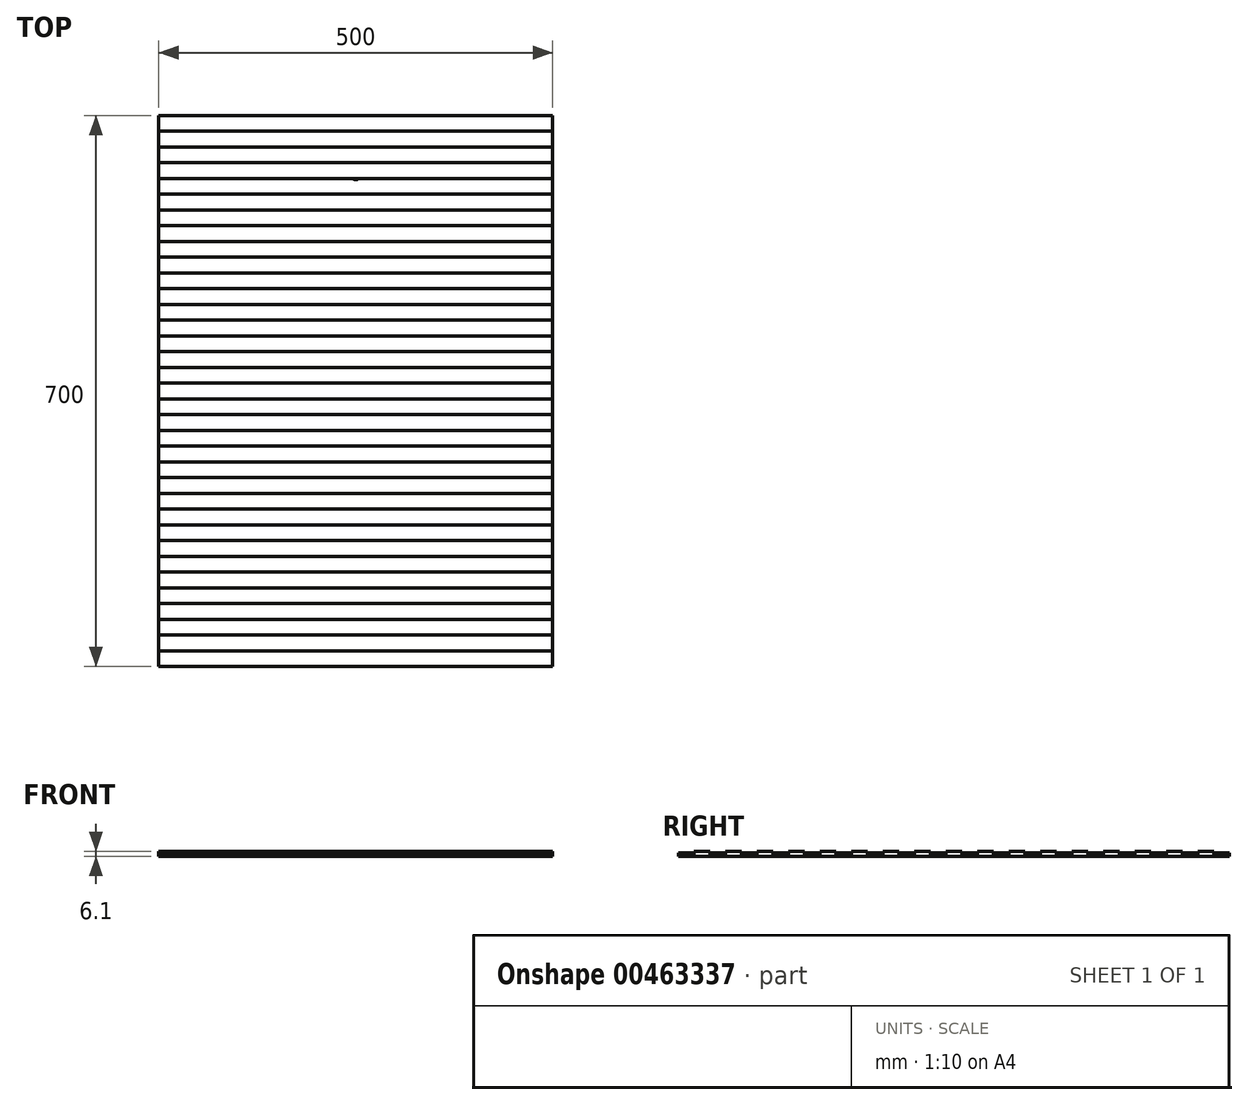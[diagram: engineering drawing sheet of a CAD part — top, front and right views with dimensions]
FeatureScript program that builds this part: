
annotation { "Feature Type Name" : "Feature", "Feature Type Description" : "" }
export const myFeature = defineFeature(function(context is Context, id is Id, definition is map)
    precondition{}
    {
        {
            var Q0;
            Q0=qCreatedBy(makeId("Top.planeOp"),FACE);
            var sketch = newSketch(context, id + "F0", { "sketchPlane" : qUnion([Q0])});
            skLineSegment(sketch, "E0.bottom", {"start": v(250, 350) * mm, "end": v(-250, 350) * mm});
            skLineSegment(sketch, "E0.top", {"start": v(250, -350) * mm, "end": v(-250, -350) * mm});
            skLineSegment(sketch, "E0.left", {"start": v(250, 350) * mm, "end": v(250, -350) * mm});
            skLineSegment(sketch, "E0.right", {"start": v(-250, 350) * mm, "end": v(-250, -350) * mm});
            skPoint(sketch, "E0.middle", {"position": v(0, 0) * mm});
            skLineSegment(sketch, "E1", {"start": v(-250, 330) * mm, "end": v(250, 330) * mm});
            skLineSegment(sketch, "E2", {"start": v(0, 350) * mm, "end": v(0, -350) * mm, "construction": true});
            skPoint(sketch, "E3", {"position": v(0, 325) * mm});
            skPoint(sketch, "E4", {"position": v(0, 275) * mm});
            skLineSegment(sketch, "E5.0.1.0", {"start": v(-250, 310) * mm, "end": v(250, 310) * mm});
            skLineSegment(sketch, "E5.0.2.0", {"start": v(-250, 290) * mm, "end": v(250, 290) * mm});
            skLineSegment(sketch, "E5.0.3.0", {"start": v(-250, 270) * mm, "end": v(250, 270) * mm});
            skLineSegment(sketch, "E5.0.4.0", {"start": v(-250, 250) * mm, "end": v(250, 250) * mm});
            skLineSegment(sketch, "E5.0.5.0", {"start": v(-250, 230) * mm, "end": v(250, 230) * mm});
            skLineSegment(sketch, "E5.0.6.0", {"start": v(-250, 210) * mm, "end": v(250, 210) * mm});
            skLineSegment(sketch, "E5.0.7.0", {"start": v(-250, 190) * mm, "end": v(250, 190) * mm});
            skLineSegment(sketch, "E5.0.8.0", {"start": v(-250, 170) * mm, "end": v(250, 170) * mm});
            skLineSegment(sketch, "E5.0.9.0", {"start": v(-250, 150) * mm, "end": v(250, 150) * mm});
            skLineSegment(sketch, "E5.0.10.0", {"start": v(-250, 130) * mm, "end": v(250, 130) * mm});
            skLineSegment(sketch, "E5.0.11.0", {"start": v(-250, 110) * mm, "end": v(250, 110) * mm});
            skLineSegment(sketch, "E5.0.12.0", {"start": v(-250, 90) * mm, "end": v(250, 90) * mm});
            skLineSegment(sketch, "E5.0.13.0", {"start": v(-250, 70) * mm, "end": v(250, 70) * mm});
            skLineSegment(sketch, "E5.0.14.0", {"start": v(-250, 50) * mm, "end": v(250, 50) * mm});
            skLineSegment(sketch, "E5.0.15.0", {"start": v(-250, 30) * mm, "end": v(250, 30) * mm});
            skLineSegment(sketch, "E5.0.16.0", {"start": v(-250, 10) * mm, "end": v(250, 10) * mm});
            skLineSegment(sketch, "E5.0.17.0", {"start": v(-250, -10) * mm, "end": v(250, -10) * mm});
            skLineSegment(sketch, "E5.0.18.0", {"start": v(-250, -30) * mm, "end": v(250, -30) * mm});
            skLineSegment(sketch, "E5.0.19.0", {"start": v(-250, -50) * mm, "end": v(250, -50) * mm});
            skLineSegment(sketch, "E5.0.20.0", {"start": v(-250, -70) * mm, "end": v(250, -70) * mm});
            skLineSegment(sketch, "E5.0.21.0", {"start": v(-250, -90) * mm, "end": v(250, -90) * mm});
            skLineSegment(sketch, "E5.0.22.0", {"start": v(-250, -110) * mm, "end": v(250, -110) * mm});
            skLineSegment(sketch, "E5.0.23.0", {"start": v(-250, -130) * mm, "end": v(250, -130) * mm});
            skLineSegment(sketch, "E5.0.24.0", {"start": v(-250, -150) * mm, "end": v(250, -150) * mm});
            skLineSegment(sketch, "E5.0.25.0", {"start": v(-250, -170) * mm, "end": v(250, -170) * mm});
            skLineSegment(sketch, "E5.0.26.0", {"start": v(-250, -190) * mm, "end": v(250, -190) * mm});
            skLineSegment(sketch, "E5.0.27.0", {"start": v(-250, -210) * mm, "end": v(250, -210) * mm});
            skLineSegment(sketch, "E5.0.28.0", {"start": v(-250, -230) * mm, "end": v(250, -230) * mm});
            skLineSegment(sketch, "E5.0.29.0", {"start": v(-250, -250) * mm, "end": v(250, -250) * mm});
            skLineSegment(sketch, "E5.0.30.0", {"start": v(-250, -270) * mm, "end": v(250, -270) * mm});
            skLineSegment(sketch, "E5.0.31.0", {"start": v(-250, -290) * mm, "end": v(250, -290) * mm});
            skLineSegment(sketch, "E5.0.32.0", {"start": v(-250, -310) * mm, "end": v(250, -310) * mm});
            skLineSegment(sketch, "E5.0.33.0", {"start": v(-250, -330) * mm, "end": v(250, -330) * mm});
            skLineSegment(sketch, "E5.0.34.0", {"start": v(-250, -350) * mm, "end": v(250, -350) * mm});
            skLineSegment(sketch, "E5.direction1", {"start": v(-250, 330) * mm, "end": v(-250, 330) * mm});
            skLineSegment(sketch, "E5.direction2", {"start": v(-250, 330) * mm, "end": v(-250, 310) * mm, "construction": true});
            skSolve(sketch);
        }
        {
            var Q0;
            {var subQ0=sQuery(id+"F0.wireOp",EDGE,"E0.bottom");Q0=makeQuery(id+"F0.imprint","IMPRINT",FACE,{"disambiguationData":[TD([[makeQuery(id+"F0.imprint","IMPRINT",EDGE,{"derivedFrom":subQ0}),1.0]])]});}
            var Q1;
            {var subQ0=sQuery(id+"F0.wireOp",EDGE,"E5.0.1.0");Q1=makeQuery(id+"F0.imprint","IMPRINT",FACE,{"disambiguationData":[TD([[makeQuery(id+"F0.imprint","IMPRINT",EDGE,{"derivedFrom":subQ0}),-1.0]])]});}
            var Q2;
            {var subQ0=sQuery(id+"F0.wireOp",EDGE,"E5.0.3.0");Q2=makeQuery(id+"F0.imprint","IMPRINT",FACE,{"disambiguationData":[TD([[makeQuery(id+"F0.imprint","IMPRINT",EDGE,{"derivedFrom":subQ0}),-1.0]])]});}
            var Q3;
            {var subQ0=sQuery(id+"F0.wireOp",EDGE,"E5.0.5.0");Q3=makeQuery(id+"F0.imprint","IMPRINT",FACE,{"disambiguationData":[TD([[makeQuery(id+"F0.imprint","IMPRINT",EDGE,{"derivedFrom":subQ0}),-1.0]])]});}
            var Q4;
            {var subQ0=sQuery(id+"F0.wireOp",EDGE,"E5.0.7.0");Q4=makeQuery(id+"F0.imprint","IMPRINT",FACE,{"disambiguationData":[TD([[makeQuery(id+"F0.imprint","IMPRINT",EDGE,{"derivedFrom":subQ0}),-1.0]])]});}
            var Q5;
            {var subQ0=sQuery(id+"F0.wireOp",EDGE,"E5.0.9.0");Q5=makeQuery(id+"F0.imprint","IMPRINT",FACE,{"disambiguationData":[TD([[makeQuery(id+"F0.imprint","IMPRINT",EDGE,{"derivedFrom":subQ0}),-1.0]])]});}
            var Q6;
            {var subQ0=sQuery(id+"F0.wireOp",EDGE,"E5.0.11.0");Q6=makeQuery(id+"F0.imprint","IMPRINT",FACE,{"disambiguationData":[TD([[makeQuery(id+"F0.imprint","IMPRINT",EDGE,{"derivedFrom":subQ0}),-1.0]])]});}
            var Q7;
            {var subQ0=sQuery(id+"F0.wireOp",EDGE,"E5.0.13.0");Q7=makeQuery(id+"F0.imprint","IMPRINT",FACE,{"disambiguationData":[TD([[makeQuery(id+"F0.imprint","IMPRINT",EDGE,{"derivedFrom":subQ0}),-1.0]])]});}
            var Q8;
            {var subQ0=sQuery(id+"F0.wireOp",EDGE,"E5.0.15.0");Q8=makeQuery(id+"F0.imprint","IMPRINT",FACE,{"disambiguationData":[TD([[makeQuery(id+"F0.imprint","IMPRINT",EDGE,{"derivedFrom":subQ0}),-1.0]])]});}
            var Q9;
            {var subQ0=sQuery(id+"F0.wireOp",EDGE,"E5.0.17.0");Q9=makeQuery(id+"F0.imprint","IMPRINT",FACE,{"disambiguationData":[TD([[makeQuery(id+"F0.imprint","IMPRINT",EDGE,{"derivedFrom":subQ0}),-1.0]])]});}
            var Q10;
            {var subQ0=sQuery(id+"F0.wireOp",EDGE,"E5.0.19.0");Q10=makeQuery(id+"F0.imprint","IMPRINT",FACE,{"disambiguationData":[TD([[makeQuery(id+"F0.imprint","IMPRINT",EDGE,{"derivedFrom":subQ0}),-1.0]])]});}
            var Q11;
            {var subQ0=sQuery(id+"F0.wireOp",EDGE,"E5.0.21.0");Q11=makeQuery(id+"F0.imprint","IMPRINT",FACE,{"disambiguationData":[TD([[makeQuery(id+"F0.imprint","IMPRINT",EDGE,{"derivedFrom":subQ0}),-1.0]])]});}
            var Q12;
            {var subQ0=sQuery(id+"F0.wireOp",EDGE,"E5.0.23.0");Q12=makeQuery(id+"F0.imprint","IMPRINT",FACE,{"disambiguationData":[TD([[makeQuery(id+"F0.imprint","IMPRINT",EDGE,{"derivedFrom":subQ0}),-1.0]])]});}
            var Q13;
            {var subQ0=sQuery(id+"F0.wireOp",EDGE,"E5.0.25.0");Q13=makeQuery(id+"F0.imprint","IMPRINT",FACE,{"disambiguationData":[TD([[makeQuery(id+"F0.imprint","IMPRINT",EDGE,{"derivedFrom":subQ0}),-1.0]])]});}
            var Q14;
            {var subQ0=sQuery(id+"F0.wireOp",EDGE,"E5.0.27.0");Q14=makeQuery(id+"F0.imprint","IMPRINT",FACE,{"disambiguationData":[TD([[makeQuery(id+"F0.imprint","IMPRINT",EDGE,{"derivedFrom":subQ0}),-1.0]])]});}
            var Q15;
            {var subQ0=sQuery(id+"F0.wireOp",EDGE,"E5.0.29.0");Q15=makeQuery(id+"F0.imprint","IMPRINT",FACE,{"disambiguationData":[TD([[makeQuery(id+"F0.imprint","IMPRINT",EDGE,{"derivedFrom":subQ0}),-1.0]])]});}
            var Q16;
            {var subQ0=sQuery(id+"F0.wireOp",EDGE,"E5.0.31.0");Q16=makeQuery(id+"F0.imprint","IMPRINT",FACE,{"disambiguationData":[TD([[makeQuery(id+"F0.imprint","IMPRINT",EDGE,{"derivedFrom":subQ0}),-1.0]])]});}
            var Q17;
            {var subQ2=sQuery(id+"F0.wireOp",EDGE,"E5.0.33.0");Q17=makeQuery(id+"F0.imprint","IMPRINT",FACE,{"disambiguationData":[TD([[makeQuery(id+"F0.imprint","IMPRINT",EDGE,{"derivedFrom":subQ2}),-1.0]])]});}
            extrude(context, id + "F1", {"entities" : qUnion([Q0, Q1, Q2, Q3, Q4, Q5, Q6, Q7, Q8, Q9, Q10, Q11, Q12, Q13, Q14, Q15, Q16, Q17]), "depth" : 4.5 * mm});
        }
        {
            var Q0;
            {var subQ0=sQuery(id+"F0.wireOp",EDGE,"E1");Q0=makeQuery(id+"F0.imprint","IMPRINT",FACE,{"disambiguationData":[TD([[makeQuery(id+"F0.imprint","IMPRINT",EDGE,{"derivedFrom":subQ0}),-1.0]])]});}
            var Q1;
            {var subQ0=sQuery(id+"F0.wireOp",EDGE,"E5.0.2.0");Q1=makeQuery(id+"F0.imprint","IMPRINT",FACE,{"disambiguationData":[TD([[makeQuery(id+"F0.imprint","IMPRINT",EDGE,{"derivedFrom":subQ0}),-1.0]])]});}
            var Q2;
            {var subQ0=sQuery(id+"F0.wireOp",EDGE,"E5.0.4.0");Q2=makeQuery(id+"F0.imprint","IMPRINT",FACE,{"disambiguationData":[TD([[makeQuery(id+"F0.imprint","IMPRINT",EDGE,{"derivedFrom":subQ0}),-1.0]])]});}
            var Q3;
            {var subQ0=sQuery(id+"F0.wireOp",EDGE,"E5.0.6.0");Q3=makeQuery(id+"F0.imprint","IMPRINT",FACE,{"disambiguationData":[TD([[makeQuery(id+"F0.imprint","IMPRINT",EDGE,{"derivedFrom":subQ0}),-1.0]])]});}
            var Q4;
            {var subQ0=sQuery(id+"F0.wireOp",EDGE,"E5.0.8.0");Q4=makeQuery(id+"F0.imprint","IMPRINT",FACE,{"disambiguationData":[TD([[makeQuery(id+"F0.imprint","IMPRINT",EDGE,{"derivedFrom":subQ0}),-1.0]])]});}
            var Q5;
            {var subQ0=sQuery(id+"F0.wireOp",EDGE,"E5.0.10.0");Q5=makeQuery(id+"F0.imprint","IMPRINT",FACE,{"disambiguationData":[TD([[makeQuery(id+"F0.imprint","IMPRINT",EDGE,{"derivedFrom":subQ0}),-1.0]])]});}
            var Q6;
            {var subQ0=sQuery(id+"F0.wireOp",EDGE,"E5.0.12.0");Q6=makeQuery(id+"F0.imprint","IMPRINT",FACE,{"disambiguationData":[TD([[makeQuery(id+"F0.imprint","IMPRINT",EDGE,{"derivedFrom":subQ0}),-1.0]])]});}
            var Q7;
            {var subQ0=sQuery(id+"F0.wireOp",EDGE,"E5.0.14.0");Q7=makeQuery(id+"F0.imprint","IMPRINT",FACE,{"disambiguationData":[TD([[makeQuery(id+"F0.imprint","IMPRINT",EDGE,{"derivedFrom":subQ0}),-1.0]])]});}
            var Q8;
            {var subQ0=sQuery(id+"F0.wireOp",EDGE,"E5.0.16.0");Q8=makeQuery(id+"F0.imprint","IMPRINT",FACE,{"disambiguationData":[TD([[makeQuery(id+"F0.imprint","IMPRINT",EDGE,{"derivedFrom":subQ0}),-1.0]])]});}
            var Q9;
            {var subQ0=sQuery(id+"F0.wireOp",EDGE,"E5.0.18.0");Q9=makeQuery(id+"F0.imprint","IMPRINT",FACE,{"disambiguationData":[TD([[makeQuery(id+"F0.imprint","IMPRINT",EDGE,{"derivedFrom":subQ0}),-1.0]])]});}
            var Q10;
            {var subQ0=sQuery(id+"F0.wireOp",EDGE,"E5.0.20.0");Q10=makeQuery(id+"F0.imprint","IMPRINT",FACE,{"disambiguationData":[TD([[makeQuery(id+"F0.imprint","IMPRINT",EDGE,{"derivedFrom":subQ0}),-1.0]])]});}
            var Q11;
            {var subQ0=sQuery(id+"F0.wireOp",EDGE,"E5.0.22.0");Q11=makeQuery(id+"F0.imprint","IMPRINT",FACE,{"disambiguationData":[TD([[makeQuery(id+"F0.imprint","IMPRINT",EDGE,{"derivedFrom":subQ0}),-1.0]])]});}
            var Q12;
            {var subQ0=sQuery(id+"F0.wireOp",EDGE,"E5.0.24.0");Q12=makeQuery(id+"F0.imprint","IMPRINT",FACE,{"disambiguationData":[TD([[makeQuery(id+"F0.imprint","IMPRINT",EDGE,{"derivedFrom":subQ0}),-1.0]])]});}
            var Q13;
            {var subQ0=sQuery(id+"F0.wireOp",EDGE,"E5.0.26.0");Q13=makeQuery(id+"F0.imprint","IMPRINT",FACE,{"disambiguationData":[TD([[makeQuery(id+"F0.imprint","IMPRINT",EDGE,{"derivedFrom":subQ0}),-1.0]])]});}
            var Q14;
            {var subQ0=sQuery(id+"F0.wireOp",EDGE,"E5.0.28.0");Q14=makeQuery(id+"F0.imprint","IMPRINT",FACE,{"disambiguationData":[TD([[makeQuery(id+"F0.imprint","IMPRINT",EDGE,{"derivedFrom":subQ0}),-1.0]])]});}
            var Q15;
            {var subQ0=sQuery(id+"F0.wireOp",EDGE,"E5.0.30.0");Q15=makeQuery(id+"F0.imprint","IMPRINT",FACE,{"disambiguationData":[TD([[makeQuery(id+"F0.imprint","IMPRINT",EDGE,{"derivedFrom":subQ0}),-1.0]])]});}
            var Q16;
            {var subQ0=sQuery(id+"F0.wireOp",EDGE,"E5.0.32.0");Q16=makeQuery(id+"F0.imprint","IMPRINT",FACE,{"disambiguationData":[TD([[makeQuery(id+"F0.imprint","IMPRINT",EDGE,{"derivedFrom":subQ0}),-1.0]])]});}
            extrude(context, id + "F2", {"entities" : qUnion([Q0, Q1, Q2, Q3, Q4, Q5, Q6, Q7, Q8, Q9, Q10, Q11, Q12, Q13, Q14, Q15, Q16]), "depth" : 6.1 * mm});
        }
        {
            var Q0;
            Q0=sQuery(id+"F0.wireOp",VERTEX,"E3");
            var Q1;
            Q1=sQuery(id+"F0.wireOp",VERTEX,"E4");
            var Q2;
            Q2=makeQuery(id+"F1.opExtrude","SWEPT_BODY",BODY,{"disambiguationData":[OSD([sQuery(id+"F0.wireOp",EDGE,"E0.left"),sQuery(id+"F0.wireOp",EDGE,"E0.right"),sQuery(id+"F0.wireOp",EDGE,"E5.0.3.0"),sQuery(id+"F0.wireOp",EDGE,"E5.0.4.0")])]});
            hole(context, id + "F3", {"style" : HoleStyle.SIMPLE, "endStyle" : HoleEndStyle.THROUGH, "oppositeDirection" : true, "holeDiameter" : 13 * mm, "tappedDepth" : 12 * mm, "tapClearance" : 3, "locations" : qUnion([Q0, Q1]), "scope" : qUnion([Q2])});
        }
    });
